# Revit family: HVAC-Other- ANJOS Ventilation-CTM 125
name_source: partatom
category: Air Terminals
units: mm (PartAtom-declared; Revit-internal decimal feet)

## family parameters
Always vertical = Yes
Cut with Voids When Loaded = No
Maintain Annotation Orientation = No
Part Type = Normal
Room Calculation Point = No
Round Connector Dimension = Use Diameter
Shared = No
Work Plane-Based = No

## types (2) — shared parameters
Cap dimensions (mm) = 200x250
Cap height (mm) = 82
Connection diameter = 125 mm  [stored 0.410105 ft]
Extract air flow at 20 Pa (m3/h) = 295
Flow rate = 44.4 L/s
Installation instructions URL link = https://www.airflow.com
Lead dimensions (mm) = 500x400
Manufacturer = Airflow
Manufacturer's name = Airflow
Material 1 = ANJ010016 1
Material 2 = ANJ010016 2
Material 4 = ANJ010016 4
Pressure = 100.0 Pa
Product URL link = https://www.airflow.com
Roof height (mm) = 140
Supply air flow at 20 Pa (m3/h) = 160
zero-valued in all types: Default Elevation

## per-type parameters (varying)
| type | Manufacturer's URL link | Materiall 3 | Model | Part number | Product name | URL |
| 125mm dia Terracotta Roof Terminal | http://www.airflow.com | ANJ010016 3 | 125mm Terracotta Roof Terminal | 90001356 | 125mm Terracotta Roof Terminal | http://www.airflow.com |
| 125mm dia Slate Roof Terminal | http://wwwairflow.com | ANJ010016 3' | 125mm Slate Roof Terrminal | 90001355 | 125mm Slate Roof Terminal | http://wwwairflow.com |

note: [stored X ft] marks values corroborated as IEEE doubles in the binary element streams (Revit-internal decimal feet)

## geometry (parser evidence)
native form markers: Sweep x2
no freeform markers — native parametric forms only
